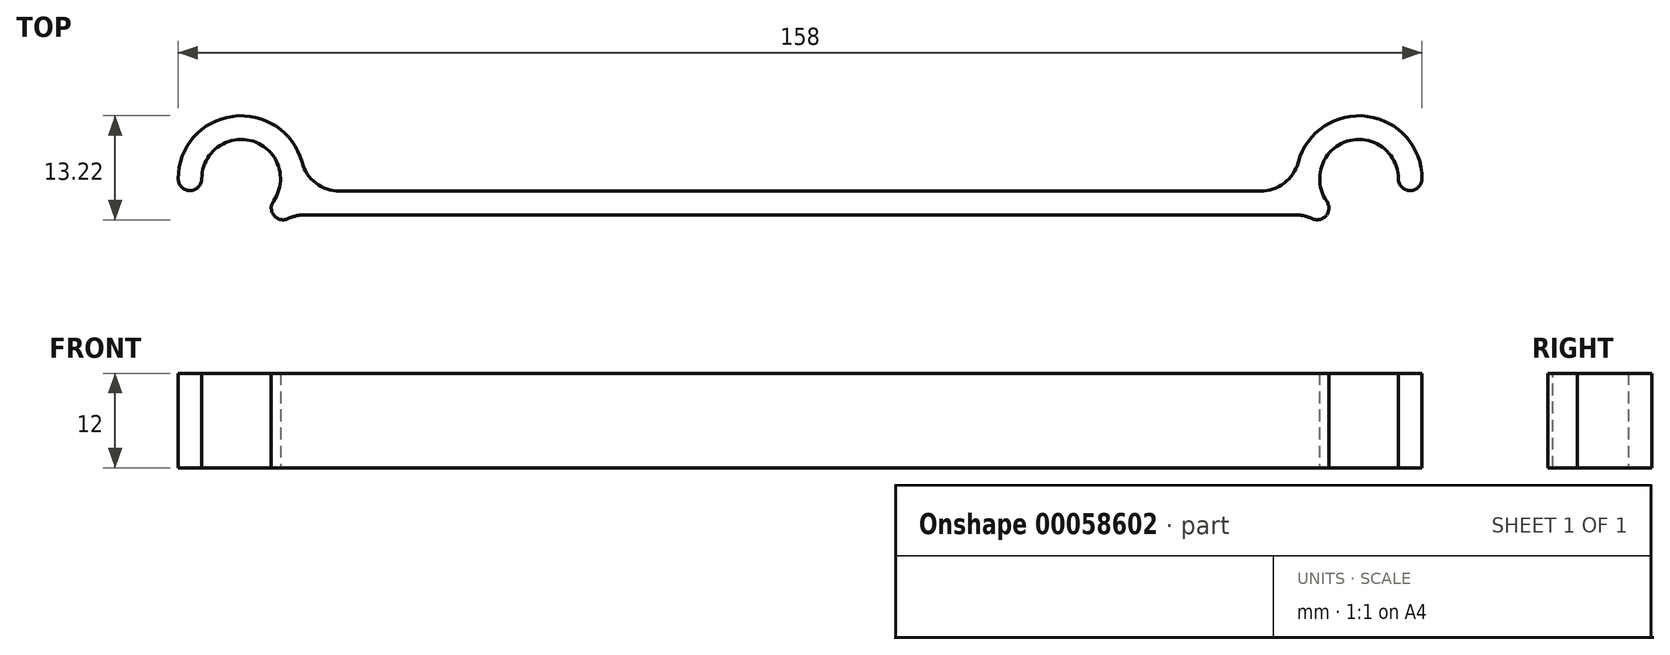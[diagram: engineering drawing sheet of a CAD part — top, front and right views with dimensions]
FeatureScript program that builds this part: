
annotation { "Feature Type Name" : "Feature", "Feature Type Description" : "" }
export const myFeature = defineFeature(function(context is Context, id is Id, definition is map)
    precondition{}
    {
        {
            var Q0;
            Q0=qCreatedBy(makeId("Top.planeOp"),FACE);
            var sketch = newSketch(context, id + "F0", { "sketchPlane" : qUnion([Q0])});
            skArc(sketch, "E0", {"start": v(-66.9, -2.86) * mm, "mid": v(-69.5, 4.77) * mm, "end": v(-76, 0) * mm});
            skArc(sketch, "E1", {"start": v(76, 0) * mm, "mid": v(69.5, 4.77) * mm, "end": v(66.9, -2.86) * mm});
            skArc(sketch, "E2", {"start": v(-63.16, -1.58) * mm, "mid": v(-70.2, 7.96) * mm, "end": v(-79, 0) * mm});
            skArc(sketch, "E3", {"start": v(79, 0) * mm, "mid": v(70.2, 7.96) * mm, "end": v(63.16, -1.58) * mm});
            skLineSegment(sketch, "E4", {"start": v(-64.44, -4.58) * mm, "end": v(64.44, -4.58) * mm});
            skLineSegment(sketch, "E5", {"start": v(-63.16, -1.58) * mm, "end": v(63.16, -1.58) * mm});
            skArc(sketch, "E6", {"start": v(-66.9, -2.86) * mm, "mid": v(-66.53, -4.95) * mm, "end": v(-64.44, -4.58) * mm});
            skArc(sketch, "E7", {"start": v(64.44, -4.58) * mm, "mid": v(66.53, -4.95) * mm, "end": v(66.9, -2.86) * mm});
            skPoint(sketch, "E8.orphan", {"position": v(66.9, -2.86) * mm});
            skLineSegment(sketch, "E9", {"start": v(-76, 0) * mm, "end": v(-77.5, 0) * mm});
            skArc(sketch, "E10", {"start": v(-79, 0) * mm, "mid": v(-77.5, -1.5) * mm, "end": v(-76, 0) * mm});
            skArc(sketch, "E11", {"start": v(76, 0) * mm, "mid": v(77.5, -1.5) * mm, "end": v(79, 0) * mm});
            skPoint(sketch, "E12.orphan", {"position": v(79, 0) * mm});
            skSolve(sketch);
        }
        {
            var Q0;
            Q0=makeQuery(id+"F0.imprint","IMPRINT",FACE,{"disambiguationData":[TD([[makeQuery(id+"F0.imprint","IMPRINT",EDGE,{"derivedFrom":sQuery(id+"F0.wireOp",EDGE,"E0")}),-1.0]])]});
            extrude(context, id + "F1", {"entities" : qUnion([Q0]), "depth" : 12 * mm});
        }
        {
            var Q0;
            Q0=makeQuery(id+"F1.opExtrude","SWEPT_EDGE",EDGE,{"disambiguationData":[OSD([sQuery(id+"F0.wireOp",EDGE,"E2"),sQuery(id+"F0.wireOp",EDGE,"E5")])]});
            var Q1;
            Q1=makeQuery(id+"F1.opExtrude","SWEPT_EDGE",EDGE,{"disambiguationData":[OSD([sQuery(id+"F0.wireOp",EDGE,"E3"),sQuery(id+"F0.wireOp",EDGE,"E5")])]});
            var Q2;
            Q2=makeQuery(id+"F1.opExtrude","SWEPT_EDGE",EDGE,{"disambiguationData":[OSD([sQuery(id+"F0.wireOp",EDGE,"E4"),sQuery(id+"F0.wireOp",EDGE,"E7")])]});
            var Q3;
            Q3=makeQuery(id+"F1.opExtrude","SWEPT_EDGE",EDGE,{"disambiguationData":[OSD([sQuery(id+"F0.wireOp",EDGE,"E4"),sQuery(id+"F0.wireOp",EDGE,"E6")])]});
            fillet(context, id + "F2", {"entities" : qUnion([Q0, Q1, Q2, Q3]), "radius" : 5 * mm, "tangentPropagation" : true, "allowEdgeOverflow" : false});
        }
    });
